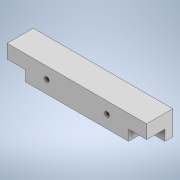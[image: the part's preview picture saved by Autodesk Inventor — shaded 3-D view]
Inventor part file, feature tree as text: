
AUTODESK INVENTOR PART (.ipt)
format: ipt  version: 2020 (Build 240168000, 168)  size: 201,728 bytes
history: native  units: mm
features: sketch x5, other x4, projected_geometry x4, extrude x3, hole x2
ambient origin geometry x8: Origin, YZ Plane, XZ Plane, XY Plane, X Axis, Y Axis, Z Axis, Center Point
bodies: Body1 (feature_tree)
feature tree (18):
  other  "작업 평면1"
  extrude  "돌출3"  Depth=13.0mm TaperAngle=0.0deg
  other  "작업 평면2"
  extrude  "돌출4"  Depth=30.0mm TaperAngle=0.0deg
  hole  "구멍1"  [1 undecoded]
  other  "작업 평면4"
  hole  "구멍2"  [1 undecoded]
  extrude  "돌출5"  Depth=30.0mm
  sketch  "스케치3"
  sketch  "스케치4"
  sketch  "스케치5"
  projected_geometry  "투영된 루프4"
  sketch  "스케치6"
  projected_geometry  "투영된 루프9"
  projected_geometry  "투영된 루프10"
  sketch  "스케치7"
  projected_geometry  "투영된 루프11"
  other  "솔리드2"
note: 2 required parameter values undecoded (feature->parameter linkage not recoverable at this tier; creation-order binding heuristic only, values carry confidence <= 0.55)
